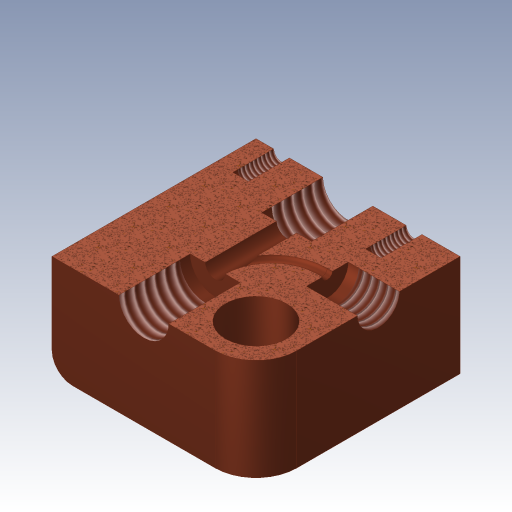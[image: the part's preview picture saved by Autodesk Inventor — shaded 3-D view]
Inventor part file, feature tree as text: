
AUTODESK INVENTOR PART (.ipt)
format: ipt  version: 2023.3 (Build 273359000, 359)  size: 302,080 bytes
history: native  units: in
note: dims shown in document units (in); Inventor stores cm internally (conversion verified against a paired STEP export)
features: hole x6, sketch x5, fillet x2, extrude x1, sweep x1
ambient origin geometry x8: Origin, YZ Plane, XZ Plane, XY Plane, X Axis, Y Axis, Z Axis, Center Point
bodies: Body1 (feature_tree)
feature tree (15):
  sketch  "Skizze3"  dims[d4=0.7874in d5=0.7874in]
  extrude  "Extrusion3"  Depth=0.7874in
  sketch  "Skizze12"  dims[d20=0.7874in d21=0.0in d68=0.3543in]
  hole  "Bohrung4"  [1 undecoded]
  hole  "Bohrung5"  [1 undecoded]
  hole  "Bohrung7"  [1 undecoded]
  sketch  "Skizze14"  dims[d84=0.0787in d85=0.1969in d86=0.1575in d87=0.0787in d88=90.0deg d89=0.2362in d90=0.0in]
  hole  "Bohrung8"  [1 undecoded]
  sweep  "Sweeping3"
  fillet  "Rundung3"  Radius=0.2756in
  sketch  "Skizze18"  dims[d102=0.1936in d103=0.2362in d104=0.1575in d105=0.0787in d106=90.0deg d107=0.2756in d108=0.0in d115=0.2362in d116=0.1772in d117=0.1772in d118=0.0394in d119=0.2756in d120=0.315in d121=0.1969in d122=0.1628in d123=0.1575in d124=0.1575in d125=0.0787in d126=90.0deg d127=0.1969in d128=0.0in d129=0.0394in d130=0.0in d131=0.0in d188=0.1575in d192=0.5118in d194=0.1772in d195=0.1378in d196=0.248in d197=0.1575in d198=0.0787in d199=90.0deg d200=0.1181in d201=0.0in d210=0.2559in d218=0.0617in d219=0.1378in d220=0.1575in d221=0.0787in d222=90.0deg d223=0.1575in d224=0.0in d229=0.4331in d230=0.0787in]
  hole  "Bohrung13"  [1 undecoded]
  hole  "Bohrung16"  [1 undecoded]
  fillet  "Rundung4"  Radius=0.0394in
  sketch  "Skizze13"  dims[d77=0.1936in d78=0.1969in d79=0.1575in d80=0.0787in d81=90.0deg d82=0.2362in d83=0.0in]
note: 6 required parameter values undecoded (feature->parameter linkage not recoverable at this tier; creation-order binding heuristic only, values carry confidence <= 0.55)
